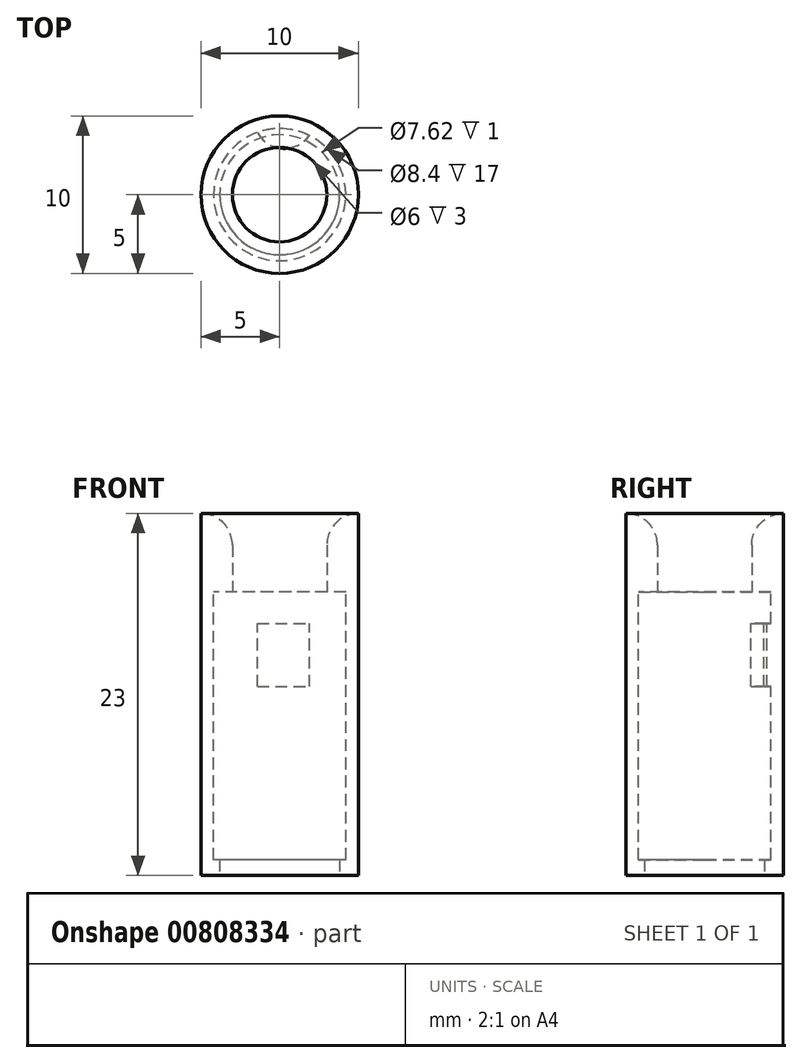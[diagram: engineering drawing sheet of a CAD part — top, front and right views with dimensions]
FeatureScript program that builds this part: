
annotation { "Feature Type Name" : "Feature", "Feature Type Description" : "" }
export const myFeature = defineFeature(function(context is Context, id is Id, definition is map)
    precondition{}
    {
        {
            var Q0;
            Q0=qCreatedBy(makeId("Top.planeOp"),FACE);
            var sketch = newSketch(context, id + "F0", { "sketchPlane" : qUnion([Q0])});
            skCircle(sketch, "E0", {"center": v(0, 0) * mm, "radius": 3.81 * mm});
            skCircle(sketch, "E1", {"center": v(0, 0) * mm, "radius": 5 * mm});
            skSolve(sketch);
        }
        {
            var Q0;
            Q0 = qSketchRegion(id + "F0", true);
            extrude(context, id + "F1", {"entities" : qUnion([Q0]), "depth" : 28 * mm, "offsetDistance" : 25 * mm});
        }
        {
            var Q0;
            Q0=makeQuery(id+"F1.opExtrude","CAP_FACE",FACE,{"disambiguationData":[OSD([sQuery(id+"F0.wireOp",EDGE,"E0"),sQuery(id+"F0.wireOp",EDGE,"E1")])],"isStart":false});
            var sketch = newSketch(context, id + "F2", { "sketchPlane" : qUnion([Q0])});
            skCircle(sketch, "E2", {"center": v(0, 0) * mm, "radius": 4.2 * mm});
            skSolve(sketch);
        }
        {
            var Q0;
            Q0=makeQuery(id+"F1.opExtrude","CAP_FACE",FACE,{"disambiguationData":[OSD([sQuery(id+"F0.wireOp",EDGE,"E0"),sQuery(id+"F0.wireOp",EDGE,"E1")])],"isStart":true});
            var sketch = newSketch(context, id + "F3", { "sketchPlane" : qUnion([Q0])});
            skCircle(sketch, "E3", {"center": v(0.16, 0) * mm, "radius": 4.2 * mm});
            skSolve(sketch);
        }
        {
            var Q0;
            Q0 = qSketchRegion(id + "F3", true);
            extrude(context, id + "F4", {"entities" : qUnion([Q0]), "operationType" : NewBodyOperationType.REMOVE, "oppositeDirection" : true, "depth" : 10 * mm, "offsetDistance" : 25 * mm});
        }
        {
            var Q0;
            Q0=makeQuery(id+"F1.opExtrude","CAP_FACE",FACE,{"disambiguationData":[OSD([sQuery(id+"F0.wireOp",EDGE,"E0"),sQuery(id+"F0.wireOp",EDGE,"E1")])],"isStart":true});
            var sketch = newSketch(context, id + "F5", { "sketchPlane" : qUnion([Q0])});
            skCircle(sketch, "E4", {"center": v(-0.3, 0) * mm, "radius": 6.63 * mm});
            skSolve(sketch);
        }
        {
            var Q0;
            Q0 = qSketchRegion(id + "F5", true);
            extrude(context, id + "F6", {"entities" : qUnion([Q0]), "operationType" : NewBodyOperationType.REMOVE, "oppositeDirection" : true, "depth" : 10 * mm, "offsetDistance" : 25 * mm});
        }
        {
            var Q0;
            Q0 = qSketchRegion(id + "F2", true);
            extrude(context, id + "F7", {"entities" : qUnion([Q0]), "operationType" : NewBodyOperationType.REMOVE, "oppositeDirection" : true, "depth" : 17 * mm, "offsetDistance" : 25 * mm});
        }
        {
            var Q0;
            Q0=makeQuery(id+"F1.opExtrude","CAP_FACE",FACE,{"disambiguationData":[OSD([sQuery(id+"F0.wireOp",EDGE,"E0"),sQuery(id+"F0.wireOp",EDGE,"E1")])],"isStart":false});
            var sketch = newSketch(context, id + "F8", { "sketchPlane" : qUnion([Q0])});
            skArc(sketch, "E5", {"start": v(-1.42, 3.95) * mm, "mid": v(0.18, 2.94) * mm, "end": v(1.88, 3.75) * mm});
            skArc(sketch, "E6", {"start": v(1.88, 3.75) * mm, "mid": v(0.25, 4.24) * mm, "end": v(-1.42, 3.95) * mm});
            skSolve(sketch);
        }
        {
            var Q0;
            Q0 = qSketchRegion(id + "F8", true);
            extrude(context, id + "F9", {"entities" : qUnion([Q0]), "operationType" : NewBodyOperationType.ADD, "oppositeDirection" : true, "depth" : 6 * mm, "offsetDistance" : 25 * mm});
        }
        {
            var Q0;
            Q0=makeQuery(id+"F9.boolean.opBoolean","MERGE",FACE,{"derivedFrom":[makeQuery(id+"F1.opExtrude","CAP_FACE",FACE,{"disambiguationData":[OSD([sQuery(id+"F0.wireOp",EDGE,"E0"),sQuery(id+"F0.wireOp",EDGE,"E1")])],"isStart":false}),makeQuery(id+"F9.opExtrude","CAP_FACE",FACE,{"disambiguationData":[OSD([sQuery(id+"F8.wireOp",EDGE,"E5"),sQuery(id+"F8.wireOp",EDGE,"E6")])],"isStart":true})]});
            var sketch = newSketch(context, id + "F10", { "sketchPlane" : qUnion([Q0])});
            skCircle(sketch, "E7", {"center": v(0, 0) * mm, "radius": 4.2 * mm});
            skSolve(sketch);
        }
        {
            var Q0;
            Q0 = qSketchRegion(id + "F10", true);
            extrude(context, id + "F11", {"entities" : qUnion([Q0]), "operationType" : NewBodyOperationType.REMOVE, "oppositeDirection" : true, "depth" : 2 * mm, "offsetDistance" : 25 * mm});
        }
        {
            var Q0;
            Q0=makeQuery(id+"F9.boolean.opBoolean","MERGE",FACE,{"derivedFrom":[makeQuery(id+"F1.opExtrude","CAP_FACE",FACE,{"disambiguationData":[OSD([sQuery(id+"F0.wireOp",EDGE,"E0"),sQuery(id+"F0.wireOp",EDGE,"E1")])],"isStart":false}),makeQuery(id+"F9.opExtrude","CAP_FACE",FACE,{"disambiguationData":[OSD([sQuery(id+"F8.wireOp",EDGE,"E5"),sQuery(id+"F8.wireOp",EDGE,"E6")])],"isStart":true})]});
            var sketch = newSketch(context, id + "F12", { "sketchPlane" : qUnion([Q0])});
            skCircle(sketch, "E8", {"center": v(0, 0) * mm, "radius": 3 * mm});
            skCircle(sketch, "E9", {"center": v(0, 0) * mm, "radius": 5 * mm});
            skSolve(sketch);
        }
        {
            var Q0;
            Q0 = qSketchRegion(id + "F12", true);
            extrude(context, id + "F13", {"entities" : qUnion([Q0]), "operationType" : NewBodyOperationType.ADD, "depth" : 5 * mm, "offsetDistance" : 25 * mm});
        }
        {
            var Q0;
            Q0=makeQuery(id+"F13.opExtrude","CAP_EDGE",EDGE,{"disambiguationData":[OSD([sQuery(id+"F12.wireOp",EDGE,"E8")])],"isStart":false});
            fillet(context, id + "F14", {"entities" : qUnion([Q0]), "radius" : 2 * mm, "tangentPropagation" : true, "allowEdgeOverflow" : false});
        }
    });
